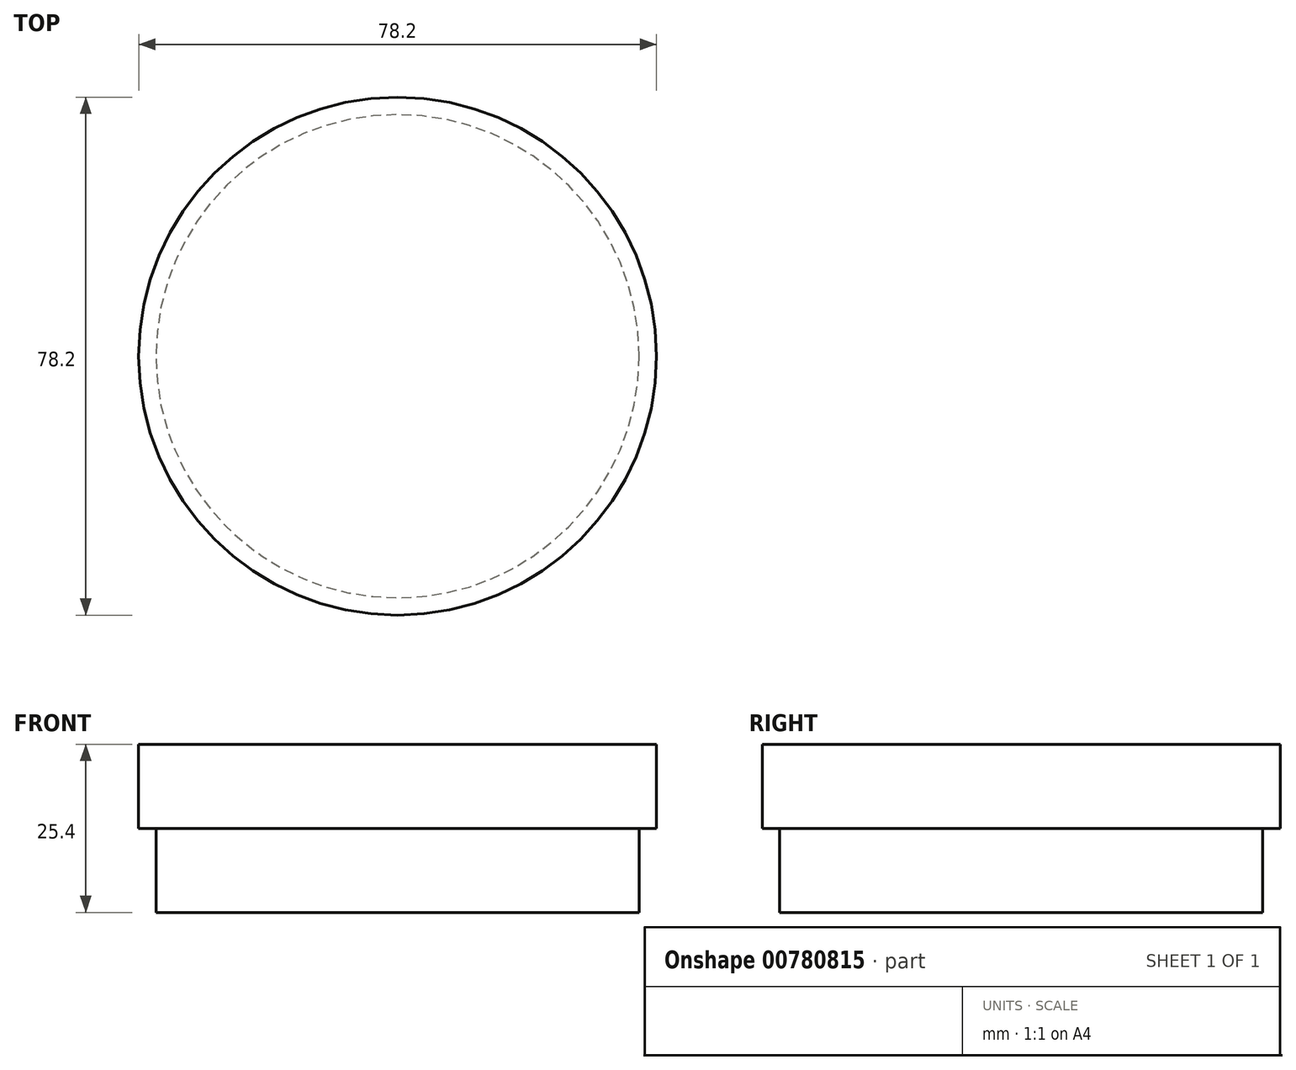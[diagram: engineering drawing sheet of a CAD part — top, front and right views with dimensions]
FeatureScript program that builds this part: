
annotation { "Feature Type Name" : "Feature", "Feature Type Description" : "" }
export const myFeature = defineFeature(function(context is Context, id is Id, definition is map)
    precondition{}
    {
        {
            var Q0;
            Q0=qCreatedBy(makeId("Top.planeOp"),FACE);
            var sketch = newSketch(context, id + "F0", { "sketchPlane" : qUnion([Q0])});
            skCircle(sketch, "E0", {"center": v(0, 0) * mm, "radius": 39.1 * mm});
            skSolve(sketch);
        }
        {
            var Q0;
            Q0 = qSketchRegion(id + "F0", true);
            extrude(context, id + "F1", {"entities" : qUnion([Q0]), "depth" : 25.4 * mm, "offsetDistance" : 25.4 * mm});
        }
        {
            var Q0;
            Q0=qCreatedBy(makeId("Top.planeOp"),FACE);
            var sketch = newSketch(context, id + "F2", { "sketchPlane" : qUnion([Q0])});
            skCircle(sketch, "E1", {"center": v(0, 0) * mm, "radius": 36.49 * mm});
            skCircle(sketch, "E2", {"center": v(0, 0) * mm, "radius": 39.1 * mm});
            skSolve(sketch);
        }
        {
            var Q0;
            Q0 = qSketchRegion(id + "F2", true);
            extrude(context, id + "F3", {"entities" : qUnion([Q0]), "operationType" : NewBodyOperationType.REMOVE, "depth" : 12.7 * mm, "offsetDistance" : 25.4 * mm});
        }
    });
